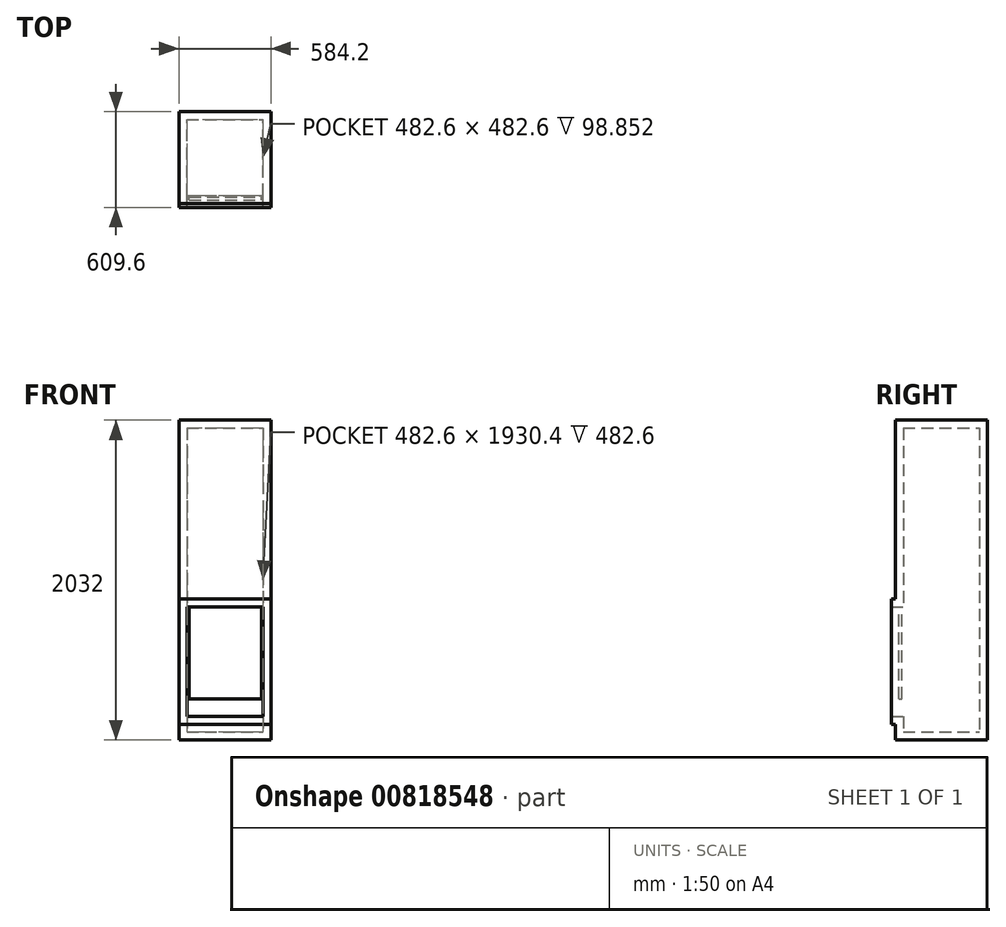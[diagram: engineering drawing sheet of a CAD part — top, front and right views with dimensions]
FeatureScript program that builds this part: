
annotation { "Feature Type Name" : "Feature", "Feature Type Description" : "" }
export const myFeature = defineFeature(function(context is Context, id is Id, definition is map)
    precondition{}
    {
        {
            var Q0;
            Q0=qCreatedBy(makeId("Front.planeOp"),FACE);
            var sketch = newSketch(context, id + "F0", { "sketchPlane" : qUnion([Q0])});
            skLineSegment(sketch, "E0.bottom", {"start": v(-290.15, 1661.71) * mm, "end": v(294.05, 1661.71) * mm});
            skLineSegment(sketch, "E0.top", {"start": v(-290.15, -370.29) * mm, "end": v(294.05, -370.29) * mm});
            skLineSegment(sketch, "E0.left", {"start": v(-290.15, 1661.71) * mm, "end": v(-290.15, -370.29) * mm});
            skLineSegment(sketch, "E0.right", {"start": v(294.05, 1661.71) * mm, "end": v(294.05, -370.29) * mm});
            skSolve(sketch);
        }
        {
            var Q0;
            Q0=makeQuery(id+"F0.imprint","IMPRINT",FACE,{"disambiguationData":[TD([[makeQuery(id+"F0.imprint","IMPRINT",EDGE,{"derivedFrom":sQuery(id+"F0.wireOp",EDGE,"E0.bottom")}),-1.0]])]});
            extrude(context, id + "F1", {"entities" : qUnion([Q0]), "depth" : 584.2 * mm, "offsetDistance" : 25.4 * mm});
        }
        {
            var Q0;
            Q0=makeQuery(id+"F1.opExtrude","CAP_FACE",FACE,{"disambiguationData":[OSD([sQuery(id+"F0.wireOp",EDGE,"E0.bottom"),sQuery(id+"F0.wireOp",EDGE,"E0.top"),sQuery(id+"F0.wireOp",EDGE,"E0.left"),sQuery(id+"F0.wireOp",EDGE,"E0.right")])],"isStart":false});
            var sketch = newSketch(context, id + "F2", { "sketchPlane" : qUnion([Q0])});
            skLineSegment(sketch, "E1.bottom", {"start": v(-290.15, 524.7) * mm, "end": v(294.05, 524.7) * mm});
            skLineSegment(sketch, "E1.top", {"start": v(-290.15, -271.44) * mm, "end": v(294.05, -271.44) * mm});
            skLineSegment(sketch, "E1.left", {"start": v(-290.15, 524.7) * mm, "end": v(-290.15, -271.44) * mm});
            skLineSegment(sketch, "E1.right", {"start": v(294.05, 524.7) * mm, "end": v(294.05, -271.44) * mm});
            skSolve(sketch);
        }
        {
            var Q0;
            Q0=makeQuery(id+"F2.imprint","IMPRINT",FACE,{"disambiguationData":[TD([[makeQuery(id+"F2.imprint","IMPRINT",EDGE,{"derivedFrom":sQuery(id+"F2.wireOp",EDGE,"E1.bottom")}),-1.0]])]});
            extrude(context, id + "F3", {"entities" : qUnion([Q0]), "operationType" : NewBodyOperationType.ADD, "depth" : 25.4 * mm, "offsetDistance" : 25.4 * mm});
        }
        {
            var Q0;
            Q0=makeQuery(id+"F3.opExtrude","CAP_FACE",FACE,{"disambiguationData":[OSD([sQuery(id+"F2.wireOp",EDGE,"E1.bottom"),sQuery(id+"F2.wireOp",EDGE,"E1.top"),sQuery(id+"F2.wireOp",EDGE,"E1.left"),sQuery(id+"F2.wireOp",EDGE,"E1.right")])],"isStart":false});
            shell(context, id + "F4", {"entities" : qUnion([Q0]), "thickness" : 50.8 * mm});
        }
        {
            var Q0;
            Q0=makeQuery(id+"F4.opShell","OFFSET_FACE",FACE,{"disambiguationData":[OSD([sQuery(id+"F2.wireOp",EDGE,"E1.bottom")])]});
            var sketch = newSketch(context, id + "F5", { "sketchPlane" : qUnion([Q0])});
            skLineSegment(sketch, "E2.bottom", {"start": v(-225.36, 561.83) * mm, "end": v(233.53, 561.83) * mm});
            skLineSegment(sketch, "E2.top", {"start": v(-225.36, 541.76) * mm, "end": v(233.53, 541.76) * mm});
            skLineSegment(sketch, "E2.left", {"start": v(-225.36, 561.83) * mm, "end": v(-225.36, 541.76) * mm});
            skLineSegment(sketch, "E2.right", {"start": v(233.53, 561.83) * mm, "end": v(233.53, 541.76) * mm});
            skSolve(sketch);
        }
        {
            var Q0;
            Q0=makeQuery(id+"F5.imprint","IMPRINT",FACE,{"disambiguationData":[TD([[makeQuery(id+"F5.imprint","IMPRINT",EDGE,{"derivedFrom":sQuery(id+"F5.wireOp",EDGE,"E2.bottom")}),-1.0]])]});
            extrude(context, id + "F6", {"entities" : qUnion([Q0]), "operationType" : NewBodyOperationType.ADD, "depth" : 581.66 * mm, "offsetDistance" : 25.4 * mm});
        }
    });
